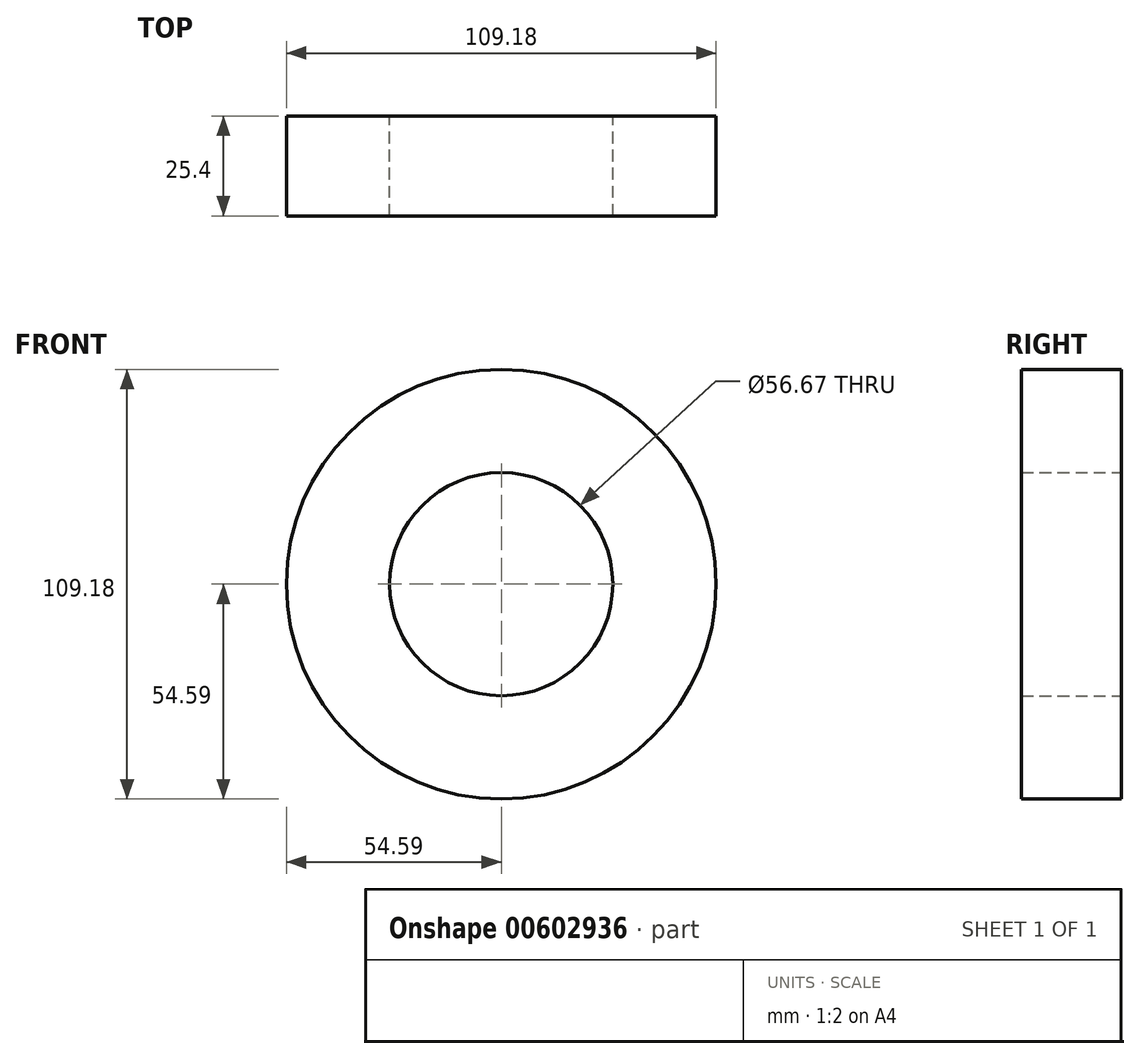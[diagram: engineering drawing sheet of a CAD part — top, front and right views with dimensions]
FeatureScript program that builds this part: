
annotation { "Feature Type Name" : "Feature", "Feature Type Description" : "" }
export const myFeature = defineFeature(function(context is Context, id is Id, definition is map)
    precondition{}
    {
        {
            var Q0;
            Q0=qCreatedBy(makeId("Front.planeOp"),FACE);
            var sketch = newSketch(context, id + "F0", { "sketchPlane" : qUnion([Q0])});
            skCircle(sketch, "E0", {"center": v(0, 0) * mm, "radius": 54.6 * mm});
            skCircle(sketch, "E1", {"center": v(0, 0) * mm, "radius": 28.34 * mm});
            skSolve(sketch);
        }
        {
            var Q0;
            Q0=makeQuery(id+"F0.imprint","IMPRINT",FACE,{"disambiguationData":[TD([[makeQuery(id+"F0.imprint","IMPRINT",EDGE,{"derivedFrom":sQuery(id+"F0.wireOp",EDGE,"E0")}),1.0]])]});
            extrude(context, id + "F1", {"entities" : qUnion([Q0]), "depth" : 25.4 * mm, "offsetDistance" : 25.4 * mm});
        }
    });
